# Revit family: Mixer-Bath Shower-Caroma Morgana with Diverter-Round Component
name_source: partatom
category: Plumbing Fixtures
revit_build: Autodesk Revit 2015 (Build: 20160512_0715(x64)
units: mm (PartAtom-declared; Revit-internal decimal feet)

## types (1)
- Chrome
    Assembly Code = D2020300
    CW Connection = Yes
    CWFU = 2
    Connector Radius = 10 mm  [stored 0.0328084 ft]
    Cost = 0 $
    Default Elevation = 1000 mm  [stored 3.28084 ft]
    HW Connection = Yes
    HWFU = 2
    Handle = Metal-Brass-Chrome
    Height_ANZRS = 168 mm  [stored 0.551181 ft]
    Length_ANZRS = 140 mm  [stored 0.459318 ft]
    Manufacturer = GWA Bathrooms & Kitchens
    Material_ANZRS = Metal-Brass-Chrome
    Model = 80309C
    ModifiedIssue_ANZRS = 20170113.01 $
    Type Comments = Caroma Morgana Bath/Shower Mixer with Diverter-140Ø Round Cover Plate
    URL = http://specify.caroma.com.au
    Vent Connection = No
    Waste Connection = No
    Width_ANZRS = 66 mm  [stored 0.216535 ft]

note: [stored X ft] marks values corroborated as IEEE doubles in the binary element streams (Revit-internal decimal feet)

## geometry (parser evidence)
native form markers: Blend x6, Sweep x2
no freeform markers — native parametric forms only
